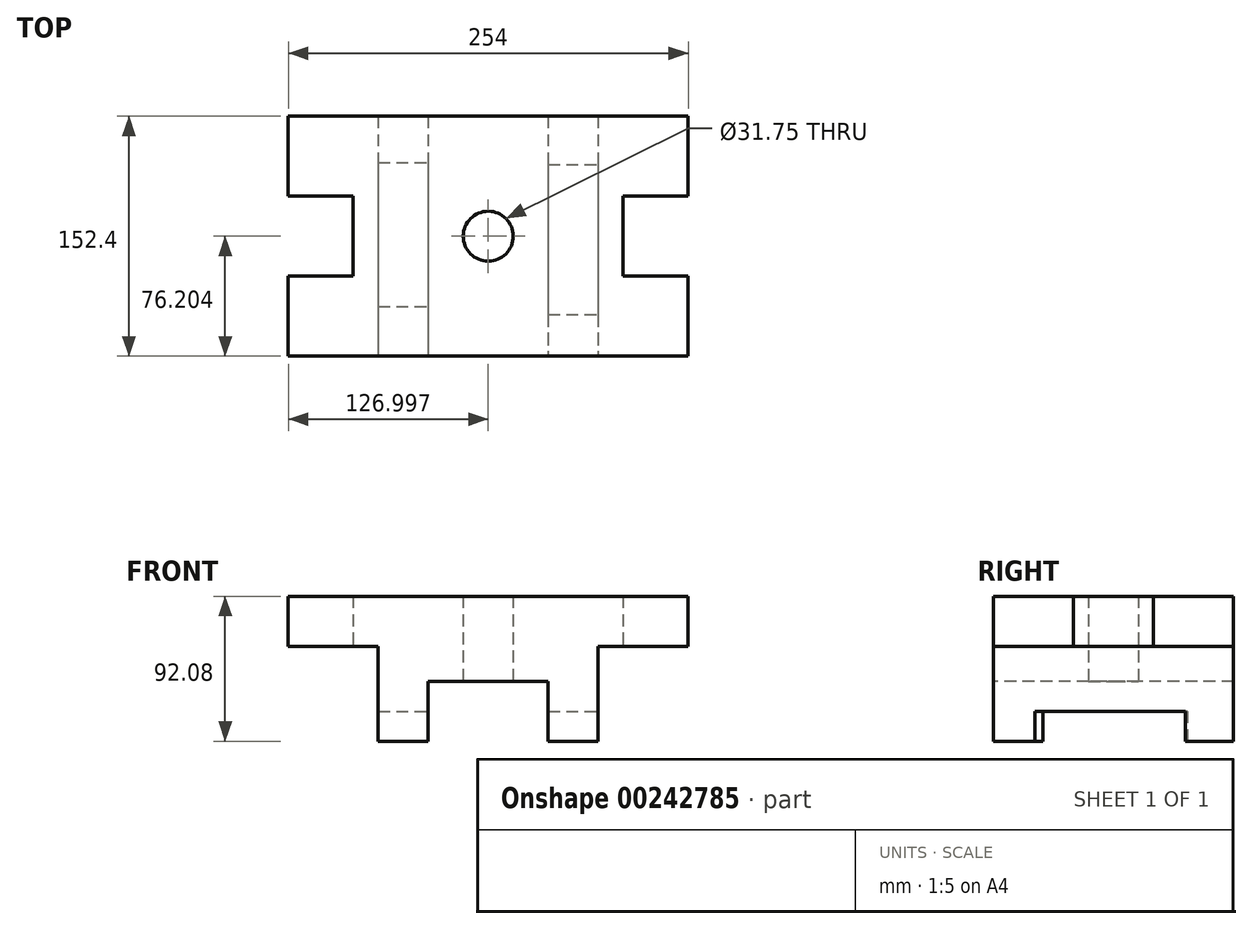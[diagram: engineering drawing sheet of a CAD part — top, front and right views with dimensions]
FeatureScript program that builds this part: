
annotation { "Feature Type Name" : "Feature", "Feature Type Description" : "" }
export const myFeature = defineFeature(function(context is Context, id is Id, definition is map)
    precondition{}
    {
        {
            var Q0;
            Q0=qCreatedBy(makeId("Top.planeOp"),FACE);
            var sketch = newSketch(context, id + "F0", { "sketchPlane" : qUnion([Q0])});
            skLineSegment(sketch, "E0.bottom", {"start": v(-146.52, 81.14) * mm, "end": v(107.48, 81.14) * mm});
            skLineSegment(sketch, "E0.top", {"start": v(-146.52, 30.34) * mm, "end": v(-105.25, 30.34) * mm});
            skLineSegment(sketch, "E0.left", {"start": v(-146.52, 81.14) * mm, "end": v(-146.52, 30.34) * mm});
            skLineSegment(sketch, "E0.right", {"start": v(107.48, 81.14) * mm, "end": v(107.48, 30.34) * mm});
            skLineSegment(sketch, "E1.bottom", {"start": v(-146.52, -20.46) * mm, "end": v(-105.25, -20.46) * mm});
            skLineSegment(sketch, "E1.top", {"start": v(-146.52, -71.26) * mm, "end": v(107.48, -71.26) * mm});
            skLineSegment(sketch, "E1.left", {"start": v(-146.52, -20.46) * mm, "end": v(-146.52, -71.26) * mm});
            skLineSegment(sketch, "E1.right", {"start": v(107.48, -20.46) * mm, "end": v(107.48, -71.26) * mm});
            skLineSegment(sketch, "E2.left", {"start": v(-105.25, 30.34) * mm, "end": v(-105.25, -20.46) * mm});
            skLineSegment(sketch, "E2.right", {"start": v(66.2, 30.34) * mm, "end": v(66.2, -20.46) * mm});
            skLineSegment(sketch, "E3.trimOffspring", {"start": v(66.2, 30.34) * mm, "end": v(107.48, 30.34) * mm});
            skLineSegment(sketch, "E4.trimOffspring", {"start": v(66.2, -20.46) * mm, "end": v(107.48, -20.46) * mm});
            skCircle(sketch, "E5", {"center": v(-19.52, 4.94) * mm, "radius": 15.88 * mm});
            skLineSegment(sketch, "E6", {"start": v(18.58, 81.14) * mm, "end": v(18.58, -71.26) * mm});
            skLineSegment(sketch, "E7", {"start": v(50.33, 81.14) * mm, "end": v(50.33, -71.26) * mm});
            skLineSegment(sketch, "E8", {"start": v(-89.37, 81.14) * mm, "end": v(-89.37, -71.26) * mm});
            skLineSegment(sketch, "E9", {"start": v(-57.62, 81.14) * mm, "end": v(-57.62, -71.26) * mm});
            skLineSegment(sketch, "E10", {"start": v(-89.37, 51.82) * mm, "end": v(-57.62, 51.82) * mm});
            skLineSegment(sketch, "E11", {"start": v(-89.37, -39.82) * mm, "end": v(-57.62, -39.82) * mm});
            skLineSegment(sketch, "E12", {"start": v(18.58, 50.48) * mm, "end": v(50.33, 50.48) * mm});
            skLineSegment(sketch, "E13", {"start": v(18.58, -44.84) * mm, "end": v(50.33, -44.84) * mm});
            skSolve(sketch);
        }
        {
            var Q0;
            Q0=makeQuery(id+"F0.imprint","IMPRINT",FACE,{"disambiguationData":[TD([[makeQuery(id+"F0.imprint","IMPRINT",EDGE,{"derivedFrom":sQuery(id+"F0.wireOp",EDGE,"E0.top")}),1.0]])]});
            var Q1;
            {var subQ5=sQuery(id+"F0.wireOp",EDGE,"E10");Q1=makeQuery(id+"F0.imprint","IMPRINT",FACE,{"disambiguationData":[TD([[makeQuery(id+"F0.imprint","IMPRINT",EDGE,{"derivedFrom":subQ5}),1.0]])]});}
            var Q2;
            {var subQ0=sQuery(id+"F0.wireOp",EDGE,"E10");Q2=makeQuery(id+"F0.imprint","IMPRINT",FACE,{"disambiguationData":[TD([[makeQuery(id+"F0.imprint","IMPRINT",EDGE,{"derivedFrom":subQ0}),-1.0]])]});}
            var Q3;
            {var subQ5=sQuery(id+"F0.wireOp",EDGE,"E11");Q3=makeQuery(id+"F0.imprint","IMPRINT",FACE,{"disambiguationData":[TD([[makeQuery(id+"F0.imprint","IMPRINT",EDGE,{"derivedFrom":subQ5}),-1.0]])]});}
            var Q4;
            Q4=makeQuery(id+"F0.imprint","IMPRINT",FACE,{"disambiguationData":[TD([[makeQuery(id+"F0.imprint","IMPRINT",EDGE,{"derivedFrom":sQuery(id+"F0.wireOp",EDGE,"E5")}),-1.0]])]});
            var Q5;
            {var subQ5=sQuery(id+"F0.wireOp",EDGE,"E12");Q5=makeQuery(id+"F0.imprint","IMPRINT",FACE,{"disambiguationData":[TD([[makeQuery(id+"F0.imprint","IMPRINT",EDGE,{"derivedFrom":subQ5}),1.0]])]});}
            var Q6;
            {var subQ0=sQuery(id+"F0.wireOp",EDGE,"E12");Q6=makeQuery(id+"F0.imprint","IMPRINT",FACE,{"disambiguationData":[TD([[makeQuery(id+"F0.imprint","IMPRINT",EDGE,{"derivedFrom":subQ0}),-1.0]])]});}
            var Q7;
            {var subQ5=sQuery(id+"F0.wireOp",EDGE,"E13");Q7=makeQuery(id+"F0.imprint","IMPRINT",FACE,{"disambiguationData":[TD([[makeQuery(id+"F0.imprint","IMPRINT",EDGE,{"derivedFrom":subQ5}),-1.0]])]});}
            var Q8;
            {var subQ8=sQuery(id+"F0.wireOp",EDGE,"E0.right");Q8=makeQuery(id+"F0.imprint","IMPRINT",FACE,{"disambiguationData":[TD([[makeQuery(id+"F0.imprint","IMPRINT",EDGE,{"derivedFrom":subQ8}),-1.0]])]});}
            extrude(context, id + "F1", {"entities" : qUnion([Q0, Q1, Q2, Q3, Q4, Q5, Q6, Q7, Q8]), "depth" : 92.07 * mm});
        }
        {
            var Q0;
            {var subQ8=sQuery(id+"F0.wireOp",EDGE,"E0.right");Q0=makeQuery(id+"F0.imprint","IMPRINT",FACE,{"disambiguationData":[TD([[makeQuery(id+"F0.imprint","IMPRINT",EDGE,{"derivedFrom":subQ8}),-1.0]])]});}
            var Q1;
            Q1=makeQuery(id+"F0.imprint","IMPRINT",FACE,{"disambiguationData":[TD([[makeQuery(id+"F0.imprint","IMPRINT",EDGE,{"derivedFrom":sQuery(id+"F0.wireOp",EDGE,"E0.top")}),1.0]])]});
            extrude(context, id + "F2", {"entities" : qUnion([Q0, Q1]), "operationType" : NewBodyOperationType.REMOVE, "depth" : 60.32 * mm});
        }
        {
            var Q0;
            Q0=makeQuery(id+"F0.imprint","IMPRINT",FACE,{"disambiguationData":[TD([[makeQuery(id+"F0.imprint","IMPRINT",EDGE,{"derivedFrom":sQuery(id+"F0.wireOp",EDGE,"E5")}),-1.0]])]});
            extrude(context, id + "F3", {"entities" : qUnion([Q0]), "operationType" : NewBodyOperationType.REMOVE, "depth" : 38.1 * mm});
        }
        {
            var Q0;
            {var subQ0=sQuery(id+"F0.wireOp",EDGE,"E12");Q0=makeQuery(id+"F0.imprint","IMPRINT",FACE,{"disambiguationData":[TD([[makeQuery(id+"F0.imprint","IMPRINT",EDGE,{"derivedFrom":subQ0}),-1.0]])]});}
            var Q1;
            {var subQ0=sQuery(id+"F0.wireOp",EDGE,"E10");Q1=makeQuery(id+"F0.imprint","IMPRINT",FACE,{"disambiguationData":[TD([[makeQuery(id+"F0.imprint","IMPRINT",EDGE,{"derivedFrom":subQ0}),-1.0]])]});}
            extrude(context, id + "F4", {"entities" : qUnion([Q0, Q1]), "operationType" : NewBodyOperationType.REMOVE, "depth" : 19.05 * mm});
        }
    });
